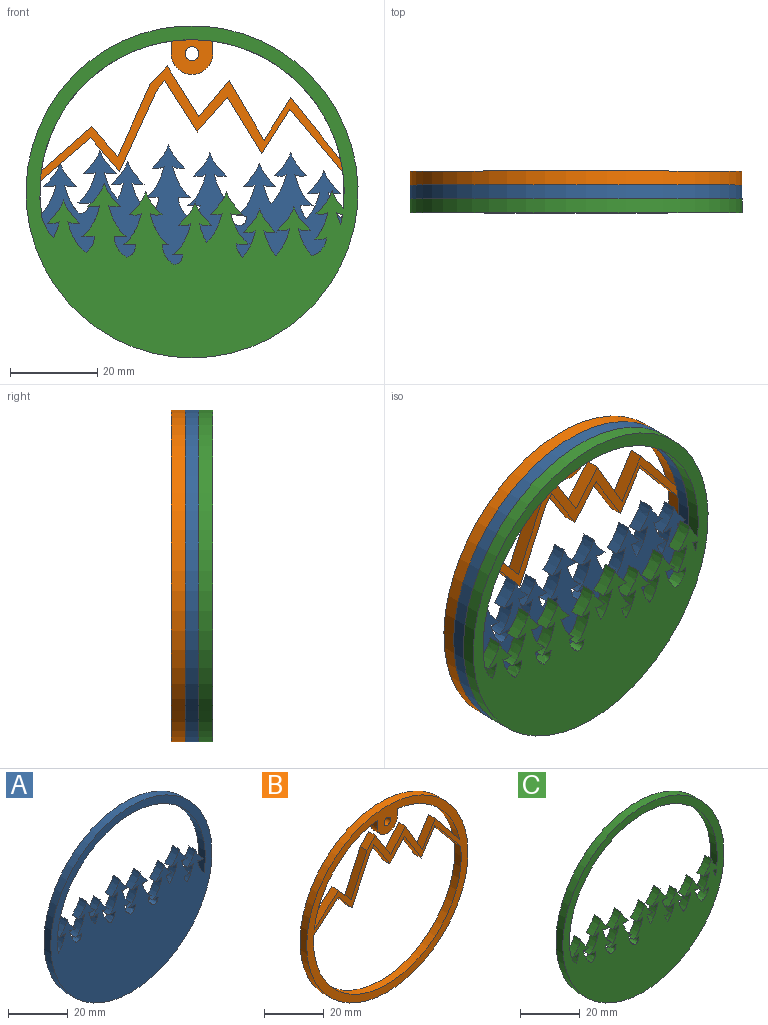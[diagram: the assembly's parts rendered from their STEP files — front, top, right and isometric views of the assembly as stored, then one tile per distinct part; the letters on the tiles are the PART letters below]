
ASSEMBLY  parts=3 mates=4
PART A: 67 faces, bbox 76.2x3.2x76.2 mm
  f0: extruded ~3.18x0.01mm, area 0.1mm2, adj f1,f63,f65,f66
  f1: extruded ~3.18x3.13mm, area 11.1mm2, adj f0,f2,f65,f66
  f2: extruded ~3.18x2.93mm, area 9.3mm2, adj f1,f3,f65,f66
  f3: extruded ~7.05x4.2mm, area 26.7mm2, adj f2,f4,f65,f66
  f4: extruded ~3.18x2.76mm, area 9mm2, adj f3,f5,f65,f66
  f5: extruded ~5.37x3.73mm, area 21mm2, adj f4,f6,f65,f66
  f6: extruded ~5.37x3.73mm, area 21mm2, adj f5,f7,f65,f66
  f7: extruded ~3.18x2.76mm, area 9mm2, adj f6,f8,f65,f66
  f8: extruded ~6.65x3.61mm, area 24.4mm2, adj f7,f9,f65,f66
  f9: extruded ~4.22x3.18mm, area 14.4mm2, adj f8,f10,f65,f66
  f10: extruded ~3.18x2.76mm, area 9mm2, adj f9,f11,f65,f66
  f11: extruded ~5.37x3.73mm, area 21mm2, adj f10,f12,f65,f66
  f12: extruded ~5.37x3.73mm, area 21mm2, adj f11,f13,f65,f66
  f13: extruded ~3.18x2.76mm, area 9mm2, adj f12,f14,f65,f66
  f14: extruded ~7.05x4.2mm, area 26.7mm2, adj f13,f15,f65,f66
  f15: extruded ~3.18x2.34mm, area 7.4mm2, adj f14,f16,f65,f66
  f16: extruded ~3.18x2.15mm, area 10.8mm2, adj f15,f17,f65,f66
  f17: extruded ~4.52x3.18mm, area 17.4mm2, adj f16,f18,f65,f66
  f18: extruded ~3.18x1.42mm, area 4.5mm2, adj f17,f19,f65,f66
  f19: extruded ~7.05x4.2mm, area 26.7mm2, adj f18,f20,f65,f66
  f20: extruded ~3.18x2.76mm, area 9mm2, adj f19,f21,f65,f66
  f21: extruded ~5.37x3.73mm, area 21mm2, adj f20,f22,f65,f66
  f22: extruded ~5.37x3.73mm, area 21mm2, adj f21,f23,f65,f66
  f23: extruded ~3.18x2.76mm, area 9mm2, adj f22,f24,f65,f66
  f24: extruded ~7.05x4.2mm, area 26.7mm2, adj f23,f25,f65,f66
  f25: extruded ~3.18x2.93mm, area 9.3mm2, adj f24,f26,f65,f66
  f26: extruded ~3.18x2.95mm, area 12.4mm2, adj f25,f27,f65,f66
  f27: extruded ~4.81x3.18mm, area 18.7mm2, adj f26,f28,f65,f66
  f28: extruded ~3.18x2.93mm, area 9.3mm2, adj f27,f29,f65,f66
  f29: extruded ~7.05x4.2mm, area 26.7mm2, adj f28,f30,f65,f66
  f30: extruded ~3.18x2.76mm, area 9mm2, adj f29,f31,f65,f66
  f31: extruded ~5.37x3.73mm, area 21mm2, adj f30,f32,f65,f66
  f32: extruded ~5.37x3.73mm, area 21mm2, adj f31,f33,f65,f66
  f33: extruded ~3.18x2.76mm, area 9mm2, adj f32,f34,f65,f66
  f34: extruded ~7.05x4.2mm, area 26.7mm2, adj f33,f35,f65,f66
  f35: extruded ~3.18x2.93mm, area 9.3mm2, adj f34,f36,f65,f66
  f36: extruded ~3.77x3.18mm, area 13.9mm2, adj f35,f37,f65,f66
  f37: extruded ~7.05x4.2mm, area 26.6mm2, adj f36,f38,f65,f66
  f38: extruded ~3.18x2.76mm, area 9mm2, adj f37,f39,f65,f66
  f39: extruded ~5.37x3.73mm, area 21mm2, adj f38,f40,f65,f66
  f40: extruded ~5.37x3.73mm, area 21mm2, adj f39,f41,f65,f66
  f41: extruded ~3.18x2.76mm, area 9mm2, adj f40,f42,f65,f66
  f42: extruded ~3.68x3.18mm, area 12.5mm2, adj f41,f43,f65,f66
  f43: extruded ~6.16x3.18mm, area 22.1mm2, adj f42,f44,f65,f66
  f44: extruded ~3.18x2.76mm, area 9mm2, adj f43,f45,f65,f66
  f45: extruded ~5.37x3.73mm, area 21mm2, adj f44,f46,f65,f66
  f46: extruded ~5.37x3.73mm, area 21mm2, adj f45,f47,f65,f66
  f47: extruded ~3.18x2.76mm, area 9mm2, adj f46,f48,f65,f66
  f48: extruded ~7.05x4.2mm, area 26.7mm2, adj f47,f49,f65,f66
  f49: extruded ~3.18x2.93mm, area 9.3mm2, adj f48,f50,f65,f66
  f50: extruded ~3.18x2.46mm, area 11.8mm2, adj f49,f51,f65,f66
  f51: extruded ~6.55x3.48mm, area 23.9mm2, adj f50,f52,f65,f66
  f52: extruded ~3.18x2.76mm, area 9mm2, adj f51,f53,f65,f66
  f53: extruded ~5.37x3.73mm, area 21mm2, adj f52,f54,f65,f66
  f54: extruded ~5.37x3.73mm, area 21mm2, adj f53,f55,f65,f66
  f55: extruded ~3.18x2.76mm, area 9mm2, adj f54,f56,f65,f66
  f56: extruded ~6.45x3.37mm, area 23.4mm2, adj f55,f57,f65,f66
  f57: cylinder r=34.92mm len=69.85mm, axis (0,1,0), area 384.1mm2, adj f56,f58,f65,f66
  f58: extruded ~6.2x3.18mm, area 22.3mm2, adj f57,f59,f65,f66
  f59: extruded ~3.18x2.76mm, area 9mm2, adj f58,f60,f65,f66
  f60: extruded ~5.37x3.73mm, area 21mm2, adj f59,f61,f65,f66
  f61: extruded ~5.37x3.73mm, area 21mm2, adj f60,f62,f65,f66
  f62: extruded ~3.18x2.76mm, area 9mm2, adj f61,f63,f65,f66
  f63: extruded ~6.1x3.18mm, area 21.8mm2, adj f0,f62,f65,f66
  f64: cylinder r=38.1mm len=76.2mm, axis (0,1,0), area 760.1mm2, adj f65,f66
  f65: plane 76.2x76.2mm, normal (0,-1,0), area 2721.2mm2, adj f0,f1,f2,f3,f4,f5,f6,f7
  f66: plane 76.2x76.2mm, normal (0,1,0), area 2721.2mm2, adj f0,f1,f2,f3,f4,f5,f6,f7
PART B: 28 faces, bbox 76.2x3.2x76.2 mm
  f0: cylinder r=34.92mm len=69.85mm, axis (0,1,0), area 370.1mm2, adj f1,f23,f26,f27
  f1: plane 11.6x9.87mm, normal (0.65,0,-0.76), area 48.3mm2, adj f0,f2,f26,f27
  f2: plane 7.76x6.61mm, normal (-0.76,0,-0.65), area 32.4mm2, adj f1,f3,f26,f27
  f3: plane 18.46x8.45mm, normal (0.91,0,-0.42), area 64.4mm2, adj f2,f4,f26,f27
  f4: plane 3.18x2.49mm, normal (0.8,0,-0.6), area 9.9mm2, adj f3,f5,f26,f27
  f5: plane 11.84x7.48mm, normal (-0.85,0,-0.53), area 44.4mm2, adj f4,f6,f26,f27
  f6: plane 7.89x6.96mm, normal (0.75,0,-0.66), area 33.4mm2, adj f5,f7,f26,f27
  f7: plane 12.87x7.89mm, normal (-0.85,0,-0.52), area 47.9mm2, adj f6,f8,f26,f27
  f8: plane 10.18x6.44mm, normal (0.85,0,-0.53), area 38.2mm2, adj f7,f23,f26,f27
  f9: plane 11.63x7.27mm, normal (0.85,0,0.53), area 43.5mm2, adj f10,f24,f26,f27
  f10: plane 4.26x3.95mm, normal (-0.73,0,0.68), area 18.4mm2, adj f9,f11,f26,f27
  f11: plane 16.5x7.4mm, normal (-0.91,0,0.41), area 57.4mm2, adj f10,f12,f26,f27
  f12: plane 6.84x6mm, normal (0.75,0,0.66), area 28.9mm2, adj f11,f13,f26,f27
  f13: plane 11.56x10.13mm, normal (-0.66,0,0.75), area 48.8mm2, adj f12,f14,f26,f27
  f14: cylinder r=34.92mm len=29.82mm, axis (0,1,0), area 143.6mm2, adj f13,f15,f26,f27
  f15: plane 3.18x2.9mm, normal (-1,0,0), area 9.2mm2, adj f14,f16,f26,f27
  f16: cylinder r=4.76mm len=9.53mm, axis (0,1,0), area 47.5mm2, adj f15,f17,f26,f27
  f17: plane 3.18x2.9mm, normal (1,0,0), area 9.2mm2, adj f16,f18,f26,f27
  f18: cylinder r=34.92mm len=29.4mm, axis (0,1,0), area 135.8mm2, adj f17,f19,f26,f27
  f19: plane 14.37x11.51mm, normal (0.78,0,0.63), area 58.4mm2, adj f18,f20,f26,f27
  f20: plane 9.76x6.13mm, normal (-0.85,0,0.53), area 36.6mm2, adj f19,f21,f26,f27
  f21: plane 13.71x7.99mm, normal (0.86,0,0.5), area 50.4mm2, adj f20,f24,f26,f27
  f22: cylinder r=1.59mm len=3.18mm, axis (0,1,0), area 31.7mm2, adj f26,f27
  f23: plane 14.59x12.21mm, normal (-0.77,0,-0.64), area 60.4mm2, adj f0,f8,f26,f27
  f24: plane 8.31x6.96mm, normal (-0.77,0,0.64), area 34.4mm2, adj f9,f21,f26,f27
  f25: cylinder r=38.1mm len=76.2mm, axis (0,1,0), area 760.1mm2, adj f26,f27
  f26: plane 76.2x76.2mm, normal (0,-1,0), area 1009.7mm2, adj f0,f1,f2,f3,f4,f5,f6,f7
  f27: plane 76.2x76.2mm, normal (0,1,0), area 1009.7mm2, adj f0,f1,f2,f3,f4,f5,f6,f7
PART C: 70 faces, bbox 76.2x3.2x76.2 mm
  f0: extruded ~3.18x1.4mm, area 4.7mm2, adj f1,f65,f68,f69
  f1: cylinder r=34.92mm len=3.18mm, axis (0,1,0), area 8mm2, adj f0,f65,f68,f69
  f2: cylinder r=34.92mm len=69.85mm, axis (0,1,0), area 379.8mm2, adj f3,f66,f68,f69
  f3: extruded ~4.1x3.18mm, area 15.5mm2, adj f2,f4,f68,f69
  f4: extruded ~5.37x3.73mm, area 21mm2, adj f3,f5,f68,f69
  f5: extruded ~3.18x2.76mm, area 9mm2, adj f4,f6,f68,f69
  f6: extruded ~6.11x3.18mm, area 21.9mm2, adj f5,f7,f68,f69
  f7: extruded ~3.18x2.67mm, area 8.7mm2, adj f6,f8,f68,f69
  f8: extruded ~4.09x3.38mm, area 18mm2, adj f7,f9,f68,f69
  f9: extruded ~6.2x3.18mm, area 22.3mm2, adj f8,f10,f68,f69
  f10: extruded ~3.18x2.76mm, area 9mm2, adj f9,f11,f68,f69
  f11: extruded ~5.37x3.73mm, area 21mm2, adj f10,f12,f68,f69
  f12: extruded ~5.37x3.73mm, area 21mm2, adj f11,f13,f68,f69
  f13: extruded ~3.18x2.76mm, area 9mm2, adj f12,f14,f68,f69
  f14: extruded ~6.11x3.18mm, area 21.9mm2, adj f13,f15,f68,f69
  f15: plane 3.18x0.19mm, normal (-0.62,0,0.79), area 0.8mm2, adj f14,f16,f68,f69
  f16: extruded ~5.74x3.18mm, area 20.3mm2, adj f15,f17,f68,f69
  f17: extruded ~3.18x2.76mm, area 9mm2, adj f16,f18,f68,f69
  f18: extruded ~5.37x3.73mm, area 21mm2, adj f17,f19,f68,f69
  f19: extruded ~5.37x3.73mm, area 21mm2, adj f18,f20,f68,f69
  f20: extruded ~3.18x2.76mm, area 9mm2, adj f19,f21,f68,f69
  f21: extruded ~6.1x3.18mm, area 21.8mm2, adj f20,f22,f68,f69
  f22: extruded ~3.18x0.01mm, area 0.1mm2, adj f21,f23,f68,f69
  f23: extruded ~3.18x3.13mm, area 11.1mm2, adj f22,f24,f68,f69
  f24: extruded ~3.18x2.93mm, area 9.3mm2, adj f23,f25,f68,f69
  f25: extruded ~7.05x4.2mm, area 26.7mm2, adj f24,f26,f68,f69
  f26: extruded ~3.18x2.76mm, area 9mm2, adj f25,f27,f68,f69
  f27: extruded ~5.37x3.73mm, area 21mm2, adj f26,f28,f68,f69
  f28: extruded ~5.37x3.73mm, area 21mm2, adj f27,f29,f68,f69
  f29: extruded ~3.18x2.76mm, area 9mm2, adj f28,f30,f68,f69
  f30: extruded ~6.65x3.61mm, area 24.4mm2, adj f29,f31,f68,f69
  f31: extruded ~4.22x3.18mm, area 14.4mm2, adj f30,f32,f68,f69
  f32: extruded ~3.18x2.76mm, area 9mm2, adj f31,f33,f68,f69
  f33: extruded ~5.37x3.73mm, area 21mm2, adj f32,f34,f68,f69
  f34: extruded ~5.37x3.73mm, area 21mm2, adj f33,f35,f68,f69
  f35: extruded ~3.18x2.76mm, area 9mm2, adj f34,f36,f68,f69
  f36: extruded ~7.05x4.2mm, area 26.7mm2, adj f35,f37,f68,f69
  f37: extruded ~3.18x2.34mm, area 7.4mm2, adj f36,f38,f68,f69
  f38: extruded ~3.18x2.15mm, area 10.8mm2, adj f37,f39,f68,f69
  f39: extruded ~4.52x3.18mm, area 17.4mm2, adj f38,f40,f68,f69
  f40: extruded ~3.18x1.42mm, area 4.5mm2, adj f39,f41,f68,f69
  f41: extruded ~7.05x4.2mm, area 26.7mm2, adj f40,f42,f68,f69
  f42: extruded ~3.18x2.76mm, area 9mm2, adj f41,f43,f68,f69
  f43: extruded ~5.37x3.73mm, area 21mm2, adj f42,f44,f68,f69
  f44: extruded ~5.37x3.73mm, area 21mm2, adj f43,f45,f68,f69
  f45: extruded ~3.18x2.76mm, area 9mm2, adj f44,f46,f68,f69
  f46: extruded ~7.05x4.2mm, area 26.7mm2, adj f45,f47,f68,f69
  f47: extruded ~3.18x2.93mm, area 9.3mm2, adj f46,f48,f68,f69
  f48: extruded ~3.18x2.95mm, area 12.4mm2, adj f47,f49,f68,f69
  f49: extruded ~4.81x3.18mm, area 18.7mm2, adj f48,f50,f68,f69
  f50: extruded ~3.18x2.93mm, area 9.3mm2, adj f49,f51,f68,f69
  f51: extruded ~7.05x4.2mm, area 26.7mm2, adj f50,f52,f68,f69
  f52: extruded ~3.18x2.76mm, area 9mm2, adj f51,f53,f68,f69
  f53: extruded ~5.37x3.73mm, area 21mm2, adj f52,f54,f68,f69
  f54: extruded ~5.37x3.73mm, area 21mm2, adj f53,f55,f68,f69
  f55: extruded ~3.18x2.76mm, area 9mm2, adj f54,f56,f68,f69
  f56: extruded ~7.05x4.2mm, area 26.7mm2, adj f55,f57,f68,f69
  f57: extruded ~3.18x2.93mm, area 9.3mm2, adj f56,f58,f68,f69
  f58: extruded ~3.77x3.18mm, area 13.9mm2, adj f57,f59,f68,f69
  f59: extruded ~7.05x4.2mm, area 26.6mm2, adj f58,f60,f68,f69
  f60: extruded ~3.18x2.76mm, area 9mm2, adj f59,f61,f68,f69
  f61: extruded ~5.37x3.73mm, area 21mm2, adj f60,f62,f68,f69
  f62: extruded ~5.37x3.73mm, area 21mm2, adj f61,f63,f68,f69
  f63: extruded ~3.18x2.76mm, area 9mm2, adj f62,f64,f68,f69
  f64: extruded ~3.68x3.18mm, area 12.5mm2, adj f63,f66,f68,f69
  f65: extruded ~3.18x2.83mm, area 9.5mm2, adj f0,f1,f68,f69
  f66: extruded ~4.5x3.18mm, area 16.6mm2, adj f2,f64,f68,f69
  f67: cylinder r=38.1mm len=76.2mm, axis (0,1,0), area 760.1mm2, adj f68,f69
  f68: plane 76.2x76.2mm, normal (0,-1,0), area 2098.5mm2, adj f0,f1,f2,f3,f4,f5,f6,f7
  f69: plane 76.2x76.2mm, normal (0,1,0), area 2098.5mm2, adj f0,f1,f2,f3,f4,f5,f6,f7
PLACE A t=(-97.51,-161.84,-24.98)mm
PLACE B t=(-97.51,-155.49,-24.98)mm
PLACE C t=(-98.01,-165.02,-27.46)mm
MATE parallel A.f66 <-> B.f26  axis (0,1,0) through (-97.73,-158.67,-35.06)mm
MATE cylindrical B.f25 <-> A.f64  axis (0,1,0) through (-97.51,-157.08,-24.98)mm
MATE parallel A.f65 <-> C.f69  axis (0,-1,0) through (-97.73,-161.84,-35.06)mm
MATE cylindrical C.f1 <-> B.f25  axis (0,1,0) through (-97.51,-163.43,-24.98)mm
